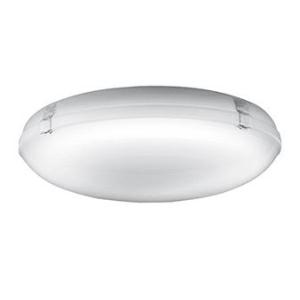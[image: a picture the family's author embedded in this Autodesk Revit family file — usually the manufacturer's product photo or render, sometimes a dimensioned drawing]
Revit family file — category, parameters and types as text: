
# Revit family: 3f_filippi_-_3f_petra_3f_filippi_-_34330_-_3f_petra_op_380_22w_led
name_source: partatom
category: Lighting Fixtures
units: mm (PartAtom-declared; Revit-internal decimal feet)

## family parameters
Cut with Voids When Loaded = No
Host = Face
Light Source = No
Part Type = Normal
Room Calculation Point = No
Round Connector Dimension = Use Diameter
Shared = No

## types (1)
- 3F Filippi - 3F Petra (1 x LED, 2978 lm, 25 W, 4000 K)
    Apparent Load = 25 VA
    Approval mark = ENEC
    CIE Flux Codes = 43 73 91 90 100
    Color Rendering = 80
    Color Temperature = 4000 K
    Control Gear = Electronic ballast
    Default Elevation = 1800 mm
    Description = ILLUMINOTECHNICAL
Luminous efficiency 100% (DLOR 90%, ULOR 10%).
Initial luminous flux of the luminaire 2978 lm.
Diffused symmetric distribution.
Installation Interdistance Transv.D = 1.26 x hu - Long.D = 1.25 x hu.
Tabular UGR (CIE 117 - 4H-8H; S=0.25H; 70/50/20): RUG 21.3 - 21.2.
Beam angle: 117° - 116°.
Luminous efficacy 119 lm/W.
Lifetime (L93/B10): 30000 h. (tq+25°C)
Lifetime (L90/B10): 50000 h. (tq+25°C)
Lifetime (L85/B10): 80000 h. (tq+25°C)
Lifetime (L80/B10): 100000 h. (tq+25°C)
Sudden decreased luminous flux after 50000 hours: 0% (C0).
Photobiological safety in compliance with IEC/TR 62778: RG0 risk exempt, (IEC 62471).
In compliance with IEC/EN 62722-2-1 - IEC/EN 62717 standards.

SOURCE
Circular LED module 22W/840.
Energy efficiency class (UE 2019/2020 - UE 2019/2015): C.
CIE 13.3 Colour rendering index: CRI >80 (R9 <50%).
IES TM-30 Fidelity Index: Rf = 84 Rg = 95.
CCT nominal colour temperature 4000 K.
Colour initial tolerance (MacAdam): SDCM 3.

MECHANICAL
Housing in glazed self-extinguishing V2 polycarbonate, UV stabilised, injection moulded.
Ecologic anti-aging injected sealing gasket.
Gear-tray reflector unit in aluminium, painted in white polyester, fixed to the housing by quick-fastening steel devices, hinged opening.
Diffuser in opal methacrylate (PMMA), injection moulded.
Snug fit safety snap-lock clips for diffuser mounting in transparent polycarbonate, screwdriver opening.
Luminaire with limited surface temperature. - D - (EN 60598-2-24)
Dimensions: diameter 380 mm, height 117 mm. Weight 1.55 kg.
IP64 protection degree.
Mechanical strength to impacts IK02 (0.2 joule).
Glow-wire test resistance 650°C.

ELECTRICAL
Halogen Free electronic wiring 230V-50/60Hz, power factor 0.90, THD <25%, constant output current, SELV, class I, 1 driver.
Power of the luminaire 25 W.
CE - IEC 60598-1 - EN 60598-1.
SAFE FLICKER: PstLM=<1 and SVM=<0.4 (IEC TR 61547-1 and IEC TR 63158), to ensure a more comfortable and safe light.
Luminaire compliant with EN 60598-2-22 for power supply from a centralised emergency system CPSS (Central Power Supply System), not incorporated in the luminaire - high risk areas excluded. The default power and flux are 100% in AC and 100% in DC.
Ambient temperature from 0°C to +25°C.
Temperature class T6 max 85°C.
Relative humidity UR: <85%.

INSTALLATION
Ceiling / Wall.

APPLICATIONS
Suitable product for food production plants (HACCP), IFS (Food Version 6), BRC (GSFS Food Version 7).
Transit areas, stairwells. Environments where a diffused lighting provides visual comfort.
Virtually in all environments compatibly with the emissions/atmospheres compromising the use of plastic materials. Not suitable for installation on surfaces subject to important vibrations, exposed to weather conditions.

WARNING
Luminaire designed for disposal/recycling at end-of-life.
Replaceable (LED only) light source by a professional. Replaceable control gear by a professional.
    Height = 117 mm
    Lamp = 1 x LED
    Lamp Light Flux = 2978 lm
    Lamp Power = 25 W
    Lamp count = 1
    Length = 380 mm
    Lifetime = 50000 h
    Luminous efficacy = 119 lm/W
    Manufacturer = 3F Filippi
    ModVariant = No
    Model = 3F Filippi - 34330 - 3F Petra OP 380 22W LED
    Mounting Place = Ceiling
    Mounting Type = Surface mounted
    Number of Poles = 1
    OnlyDefault = Yes
    Power Factor = 1
    Product Name = 3F Filippi - 3F Petra
    Product group = ceiling mounted luminaire
    ProductGroupID = 3
    Protection Class = Protection class I
    Protection Degree = IP 64
    RLX_Detail_Level = 1
    RLX_Emergency_Light_Flux = 0 lm
    RLX_Emergency_Type = 0
    RLX_Emergency_Type_DB = No
    RlxData = <blob elided: 220193 chars, md5=b289eafd>
    Socket = socket
    Standby Power = 0 W
    System Light Flux = 2978 lm
    System Power = 25 W
    Type Comments = Product without accessories
    Type Image = 3ffilippi_34330.jpg
    URL = http://relux.com
    VarID = ---
    Voltage = 0 V
    Weight = 0.00 kg
    Width = 0 mm  [stored 0 ft]

note: [stored X ft] marks values corroborated as IEEE doubles in the binary element streams (Revit-internal decimal feet)

## geometry (parser evidence)
native form markers: Blend x4, Sweep x14
no freeform markers — native parametric forms only
